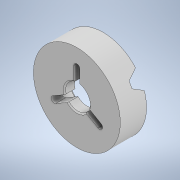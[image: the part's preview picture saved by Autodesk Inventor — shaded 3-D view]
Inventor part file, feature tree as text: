
AUTODESK INVENTOR PART (.ipt)
format: ipt  version: 2020 (Build 240168000, 168)  size: 240,128 bytes
history: native  units: mm
features: chamfer x8, extrude x4, thicken_offset x4, sketch x4, projected_geometry x3, pattern_circular x2, plane x1
ambient origin geometry x8: Origin, YZ Plane, XZ Plane, XY Plane, X Axis, Y Axis, Z Axis, Center Point
bodies: Solid1 (feature_tree)
feature tree (26):
  extrude  "Extrusion1"  Depth=21.5mm
  extrude  "Extrusion2"  Depth=6.0mm
  extrude  "Extrusion3"  Depth=2.5mm
  pattern_circular  "Circular Pattern1"  [2 undecoded]
  plane  "Work Plane1"
  extrude  "Extrusion4"  Depth=2.5mm TaperAngle=360.0deg
  pattern_circular  "Circular Pattern2"  [2 undecoded]
  chamfer  "Chamfer1"  Distance=20.0mm
  chamfer  "Chamfer2"  Distance=1.5mm
  chamfer  "Chamfer3"  Distance=2.5mm
  chamfer  "Chamfer4"  Distance=30.0mm Angle=360.0deg
  chamfer  "Chamfer5"  Distance=2.5mm Angle=30.0deg
  chamfer  "Chamfer6"  Distance=2.5mm Angle=30.0deg
  chamfer  "Chamfer7"  Distance=2.5mm Angle=30.0deg
  thicken_offset  "Thicken1"
  thicken_offset  "Thicken2"
  thicken_offset  "Thicken3"
  chamfer  "Chamfer8"  Distance=2.5mm Angle=30.0deg
  thicken_offset  "Thicken4"
  sketch  "Sketch1"  dims[d0=18.0mm d1=21.5mm]
  sketch  "Sketch2"  dims[d2=4.0mm d3=0.0mm d4=6.0mm]
  sketch  "Sketch3"  dims[d5=2.5mm d6=0.0mm d7=6.5mm]
  projected_geometry  "Projected Loop1"
  sketch  "Sketch4"  dims[d8=1.5mm d9=2.5mm d10=0.0mm d11=30.0mm d12=360.0deg d14=1.5mm d15=20.0mm d16=1.5mm d17=2.5mm d18=0.0mm d19=30.0mm d20=360.0deg d22=2.5mm d23=2.0mm d24=30.0deg d25=2.5mm d26=2.0mm d27=30.0deg d28=2.5mm d29=2.0mm d30=30.0deg d31=2.5mm d32=2.0mm d33=30.0deg d34=2.5mm d35=2.0mm d36=30.0deg d37=2.5mm d38=2.0mm d39=30.0deg d40=0.5mm d41=2.0mm d42=30.0deg d43=0.07mm d44=0.05mm d45=0.07mm d46=0.05mm d47=0.07mm d48=0.05mm d49=0.3mm d50=2.0mm d51=45.0deg d52=0.02mm d53=0.02mm]
  projected_geometry  "Projected Loop2"
  projected_geometry  "Projected Loop3"
note: 4 required parameter values undecoded (feature->parameter linkage not recoverable at this tier; creation-order binding heuristic only, values carry confidence <= 0.55)
